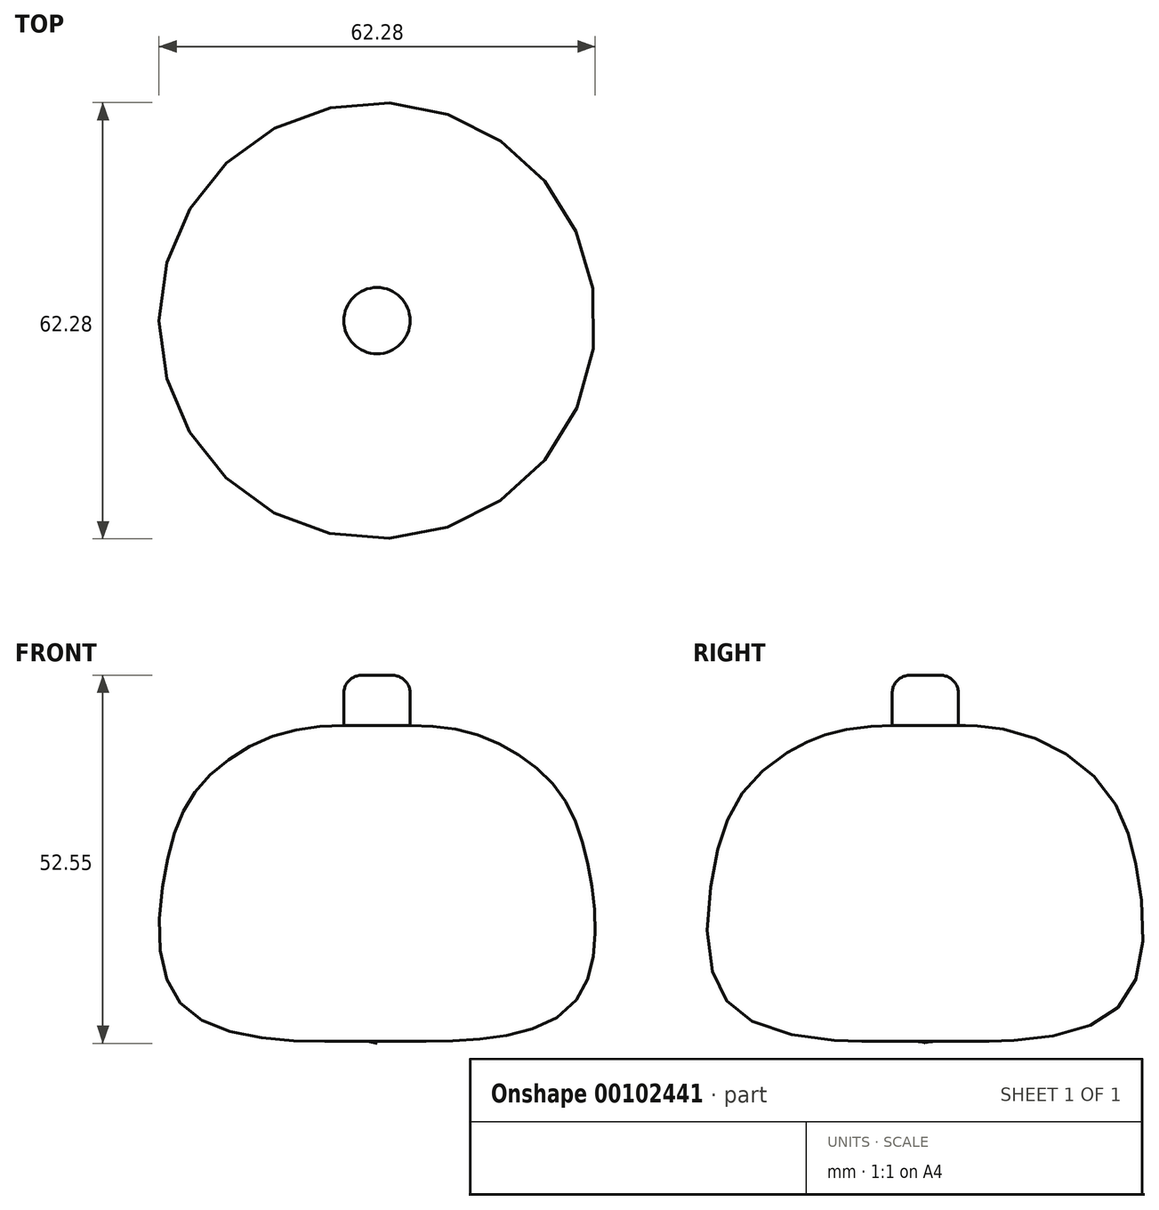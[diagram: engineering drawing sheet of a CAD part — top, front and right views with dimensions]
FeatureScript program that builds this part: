
annotation { "Feature Type Name" : "Feature", "Feature Type Description" : "" }
export const myFeature = defineFeature(function(context is Context, id is Id, definition is map)
    precondition{}
    {
        {
            var Q0;
            Q0=qCreatedBy(makeId("Front.planeOp"),FACE);
            var sketch = newSketch(context, id + "F0", { "sketchPlane" : qUnion([Q0])});
            skFitSpline(sketch, "E0", {"points": [v(0, 35.9) * mm, v(-13.13, 35.02) * mm, v(-24.82, 27.96) * mm, v(-30.12, 16.05) * mm, v(-28.13, -3.58) * mm, v(-8.28, -9.1) * mm, v(0, -9.31) * mm, v(0, -9.53) * mm], "startDerivative": vector(-84.55, 3.1) * mm, "endDerivative": vector(-4.24, -11.7) * mm});
            skLineSegment(sketch, "E1", {"start": v(0, 35.9) * mm, "end": v(0.03, -9.46) * mm});
            skSolve(sketch);
        }
        {
            var Q0;
            {var subQ0=sQuery(id+"F0.wireOp",EDGE,"E1");var subQ1=sQuery(id+"F0.wireOp",EDGE,"E0");var subQ2=makeQuery(id+"F0.imprint","INTERSECT",VERTEX,{"disambiguationData":[OD(0.0)],"derivedFrom":[subQ1,subQ0]});Q0=makeQuery(id+"F0.imprint","IMPRINT",FACE,{"disambiguationData":[TD([[makeQuery(id+"F0.imprint","IMPRINT",EDGE,{"disambiguationData":[TD([[subQ2,-1.0]])],"derivedFrom":subQ1}),1.0]])]});}
            var Q1;
            Q1=sQuery(id+"F0.wireOp",EDGE,"E1");
            revolve(context, id + "F1", {"entities" : qUnion([Q0]), "axis" : qUnion([Q1]), "revolveType" : RevolveType.FULL});
        }
        {
            var Q0;
            Q0=qCreatedBy(makeId("Top.planeOp"),FACE);
            cPlane(context, id + "F2", {"entities" : qUnion([Q0]), "cplaneType" : CPlaneType.OFFSET, "offset" : 33.02 * mm, "width" : 152.4 * mm, "height" : 152.4 * mm});
        }
        {
            var Q0;
            Q0=qCreatedBy(id+"F2.planeOp",FACE);
            var sketch = newSketch(context, id + "F3", { "sketchPlane" : qUnion([Q0])});
            skCircle(sketch, "E2", {"center": v(0, 0) * mm, "radius": 4.73 * mm});
            skSolve(sketch);
        }
        {
            var Q0;
            Q0 = qSketchRegion(id + "F3", true);
            extrude(context, id + "F4", {"entities" : qUnion([Q0]), "operationType" : NewBodyOperationType.ADD, "depth" : 10.16 * mm});
        }
        {
            var Q0;
            Q0=makeQuery(id+"F4.opExtrude","CAP_EDGE",EDGE,{"disambiguationData":[OSD([sQuery(id+"F3.wireOp",EDGE,"E2")])],"isStart":false});
            fillet(context, id + "F5", {"entities" : qUnion([Q0]), "radius" : 2.54 * mm, "tangentPropagation" : true, "allowEdgeOverflow" : false});
        }
    });
